# Revit family: UnoFloor Mixing Comfort(Control)_RFA_1
name_source: partatom
category: Pipe Accessories
units: mm (PartAtom-declared; Revit-internal decimal feet)

## family parameters
Always vertical = Yes
Cut with Voids When Loaded = No
OmniClass Number = 23.65.55.14.17
OmniClass Title = Adjusting/Controlling Valves for Liquid Services
Part Type = Valve - Breaks Into
Round Connector Dimension = Use Diameter
Shared = No
Work Plane-Based = Yes

## types (4) — shared parameters
Body Material = Danfoss Steel (Zinc Plated and Painted White)
D = 20 mm  [stored 0.0656168 ft]
Default Elevation = 1219.2 mm  [stored 4 ft]
Description = Distribution Units
H = 939 mm  [stored 3.08071 ft]
H1 = 262 mm  [stored 0.85958 ft]
H2 = 166 mm  [stored 0.544619 ft]
IfcExportAs = IfcValveType
L1 = 50 mm  [stored 0.164042 ft]
LookupTableName = Unofloor Mixing Comfort(Control)_Lookup
Manufacturer = Danfoss
Max Differential Pressure = 0.6 bar
Max Medium Temperature = 60 °C
Nominal Pressure = PN 6
Power = 0 VA
URL = https://store.danfoss.com
Voltage = 230 V
W = 110 mm  [stored 0.360892 ft]

## per-type parameters (varying)
| type | IfcExportType | Left Assembly | Model | Pack Contents | Right Assembly | Type number |
| UnoFloor Mixing Control_4L-12L | Unofloor Mixing Control Left | Yes | 088X4714,088X4715,088X4716,088X4717,088X4718,088X4720,088X4722 | Danfoss Icon2™ Master controller 230V, Actuators, Stainless steel manifold, Spacer Heat meter, AB-PM, Shunt, Circulation Pump | No | 3 |
| UnoFloor Mixing Control_4R-12R | Unofloor Mixing Control Right | No | 088X4734,088X4735,088X4736,088X4737,088X4738,088X4740,088X4742 | Danfoss Icon2™ Master controller 230V, Actuators, Stainless steel manifold, Spacer Heat meter, AB-PM, Shunt, Circulation Pump | Yes | 4 |
| UnoFloor Mixing Comfort_4L-12L | Unofloor Mixing Comfort Left | Yes | 088X4604,088X4605,088X4606,088X4607,088X4608,088X4610,088X4612 | Danfoss Icon™ Wiring center 230V, Actuators, Stainless steel manifold, Spacer Heat meter, AB-PM, Shunt, Circulation Pump | No | 1 |
| UnoFloor Mixing Comfort_4R-12R | Unofloor Mixing Comfort Right | No | 088X4624,088X4625,088X4626,088X4627,088X4628,088X4630,088X4632 | Danfoss Icon™ Wiring center 230V, Actuators, Stainless steel manifold, Spacer Heat meter, AB-PM, Shunt, Circulation Pump | Yes | 2 |

note: [stored X ft] marks values corroborated as IEEE doubles in the binary element streams (Revit-internal decimal feet)

## geometry (parser evidence)
native form markers: Sweep x1
no freeform markers — native parametric forms only
